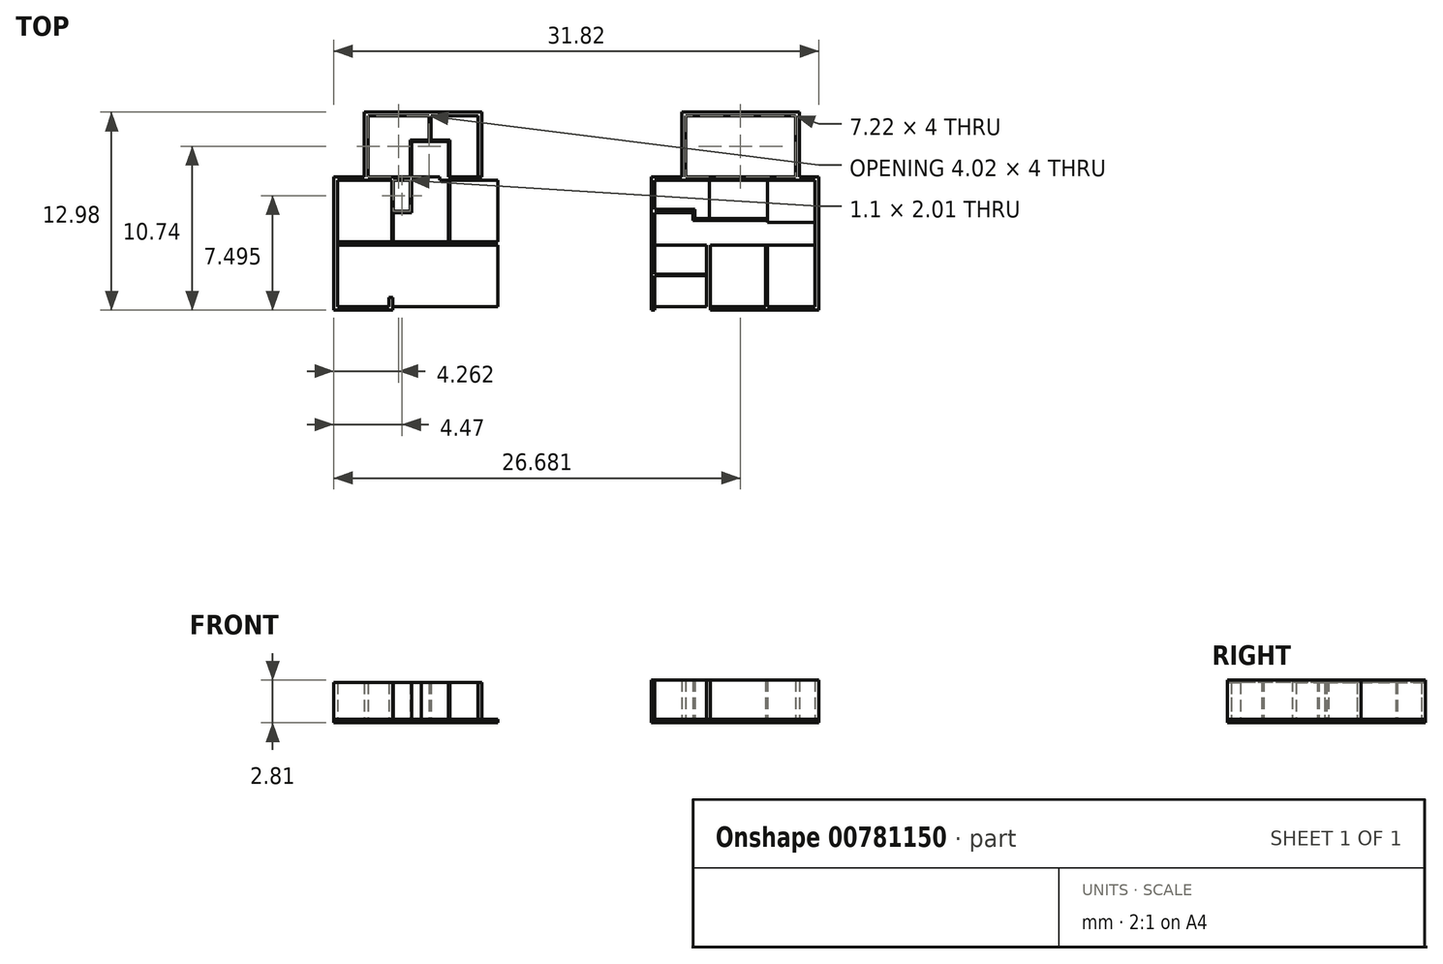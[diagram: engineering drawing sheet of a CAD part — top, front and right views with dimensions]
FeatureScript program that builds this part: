
annotation { "Feature Type Name" : "Feature", "Feature Type Description" : "" }
export const myFeature = defineFeature(function(context is Context, id is Id, definition is map)
    precondition{}
    {
        {
            var Q0;
            Q0=qCreatedBy(makeId("Top.planeOp"),FACE);
            var sketch = newSketch(context, id + "F0", { "sketchPlane" : qUnion([Q0])});
            skLineSegment(sketch, "E0.bottom", {"start": v(-5.5, 4.37) * mm, "end": v(5.5, 4.37) * mm});
            skLineSegment(sketch, "E0.top", {"start": v(-5.5, -4.37) * mm, "end": v(5.5, -4.37) * mm});
            skLineSegment(sketch, "E0.left", {"start": v(-5.5, 4.37) * mm, "end": v(-5.5, -4.37) * mm});
            skLineSegment(sketch, "E0.right", {"start": v(5.5, 4.37) * mm, "end": v(5.5, -4.37) * mm});
            skPoint(sketch, "E0.middle", {"position": v(0, 0) * mm});
            skLineSegment(sketch, "E1.bottom", {"start": v(-5.25, 4.13) * mm, "end": v(5.25, 4.13) * mm});
            skLineSegment(sketch, "E1.top", {"start": v(-5.25, -4.13) * mm, "end": v(5.25, -4.13) * mm});
            skLineSegment(sketch, "E1.left", {"start": v(-5.25, 4.13) * mm, "end": v(-5.25, -4.13) * mm});
            skLineSegment(sketch, "E1.right", {"start": v(5.25, 4.13) * mm, "end": v(5.25, -4.13) * mm});
            skLineSegment(sketch, "E2.bottom", {"start": v(-5.5, -4.37) * mm, "end": v(-1.63, -4.37) * mm});
            skLineSegment(sketch, "E2.top", {"start": v(-5.5, -7.87) * mm, "end": v(-1.63, -7.87) * mm});
            skLineSegment(sketch, "E2.left", {"start": v(-5.5, -4.37) * mm, "end": v(-5.5, -7.87) * mm});
            skLineSegment(sketch, "E2.right", {"start": v(-1.63, -4.37) * mm, "end": v(-1.63, -7.87) * mm});
            skLineSegment(sketch, "E3.bottom", {"start": v(-5.25, -4.37) * mm, "end": v(-1.87, -4.37) * mm});
            skLineSegment(sketch, "E3.top", {"start": v(-5.25, -7.63) * mm, "end": v(-1.87, -7.63) * mm});
            skLineSegment(sketch, "E3.left", {"start": v(-5.25, -4.37) * mm, "end": v(-5.25, -7.63) * mm});
            skLineSegment(sketch, "E3.right", {"start": v(-1.87, -4.37) * mm, "end": v(-1.87, -7.63) * mm});
            skLineSegment(sketch, "E4", {"start": v(-5.25, 0.12) * mm, "end": v(5.25, 0.12) * mm});
            skLineSegment(sketch, "E5", {"start": v(5.25, 0.12) * mm, "end": v(5.25, -0.12) * mm});
            skLineSegment(sketch, "E6", {"start": v(5.25, -0.12) * mm, "end": v(-5.25, -0.12) * mm});
            skLineSegment(sketch, "E7", {"start": v(-5.25, -0.12) * mm, "end": v(-5.25, 0.12) * mm});
            skLineSegment(sketch, "E8.bottom", {"start": v(-1.63, -4.37) * mm, "end": v(-1.87, -4.37) * mm});
            skLineSegment(sketch, "E8.top", {"start": v(-1.63, -3.53) * mm, "end": v(-1.87, -3.53) * mm});
            skLineSegment(sketch, "E8.left", {"start": v(-1.63, -4.37) * mm, "end": v(-1.63, -3.53) * mm});
            skLineSegment(sketch, "E8.right", {"start": v(-1.87, -4.37) * mm, "end": v(-1.87, -3.53) * mm});
            skLineSegment(sketch, "E9", {"start": v(-5.25, -4.13) * mm, "end": v(-5.25, -4.37) * mm});
            skLineSegment(sketch, "E10", {"start": v(-1.87, -4.13) * mm, "end": v(-1.87, -4.37) * mm});
            skLineSegment(sketch, "E11.bottom", {"start": v(4.2, 4.37) * mm, "end": v(-3.49, 4.37) * mm});
            skLineSegment(sketch, "E11.top", {"start": v(4.2, 8.61) * mm, "end": v(-3.49, 8.61) * mm});
            skLineSegment(sketch, "E11.left", {"start": v(4.2, 4.37) * mm, "end": v(4.2, 8.61) * mm});
            skLineSegment(sketch, "E11.right", {"start": v(-3.49, 4.37) * mm, "end": v(-3.49, 8.61) * mm});
            skLineSegment(sketch, "E12.bottom", {"start": v(-3.25, 4.37) * mm, "end": v(3.97, 4.37) * mm});
            skLineSegment(sketch, "E12.top", {"start": v(-3.25, 8.37) * mm, "end": v(3.97, 8.37) * mm});
            skLineSegment(sketch, "E12.left", {"start": v(-3.25, 4.37) * mm, "end": v(-3.25, 8.37) * mm});
            skLineSegment(sketch, "E12.right", {"start": v(3.97, 4.37) * mm, "end": v(3.97, 8.37) * mm});
            skLineSegment(sketch, "E13", {"start": v(-1.68, 4.13) * mm, "end": v(-1.68, 0.12) * mm});
            skLineSegment(sketch, "E14", {"start": v(-1.68, 0.12) * mm, "end": v(-1.58, 0.12) * mm});
            skLineSegment(sketch, "E15", {"start": v(-1.58, 0.12) * mm, "end": v(-1.58, 4.13) * mm});
            skLineSegment(sketch, "E16", {"start": v(-1.58, 4.13) * mm, "end": v(2.02, 4.13) * mm});
            skLineSegment(sketch, "E17", {"start": v(2.02, 4.13) * mm, "end": v(2.02, 0.12) * mm});
            skLineSegment(sketch, "E18", {"start": v(2.02, 0.12) * mm, "end": v(2.12, 0.12) * mm});
            skLineSegment(sketch, "E19", {"start": v(2.12, 0.12) * mm, "end": v(2.12, 4.13) * mm});
            skLineSegment(sketch, "E20", {"start": v(2.12, 4.13) * mm, "end": v(2.02, 4.13) * mm});
            skLineSegment(sketch, "E21", {"start": v(-1.58, 4.13) * mm, "end": v(-1.68, 4.13) * mm});
            skLineSegment(sketch, "E22", {"start": v(-0.48, 4.13) * mm, "end": v(-0.48, 2.12) * mm});
            skLineSegment(sketch, "E23", {"start": v(-0.48, 2.12) * mm, "end": v(-1.58, 2.12) * mm});
            skLineSegment(sketch, "E24", {"start": v(-1.58, 2.12) * mm, "end": v(-1.58, 2.02) * mm});
            skLineSegment(sketch, "E25", {"start": v(-1.58, 2.02) * mm, "end": v(-0.38, 2.02) * mm});
            skLineSegment(sketch, "E26", {"start": v(-0.38, 2.02) * mm, "end": v(-0.38, 4.13) * mm});
            skLineSegment(sketch, "E27", {"start": v(-0.38, 4.13) * mm, "end": v(-0.48, 4.13) * mm});
            skLineSegment(sketch, "E28", {"start": v(1.45, 4.37) * mm, "end": v(1.45, 4.13) * mm});
            skLineSegment(sketch, "E29", {"start": v(0.25, 4.37) * mm, "end": v(0.25, 4.13) * mm});
            skLineSegment(sketch, "E30", {"start": v(2.12, 4.37) * mm, "end": v(2.12, 6.54) * mm});
            skLineSegment(sketch, "E31", {"start": v(-0.38, 4.37) * mm, "end": v(-0.48, 4.37) * mm});
            skLineSegment(sketch, "E32", {"start": v(-0.38, 6.67) * mm, "end": v(2.02, 6.67) * mm});
            skLineSegment(sketch, "E33", {"start": v(2.02, 6.67) * mm, "end": v(2.02, 4.37) * mm});
            skLineSegment(sketch, "E34", {"start": v(-0.48, 6.77) * mm, "end": v(2.12, 6.77) * mm});
            skLineSegment(sketch, "E35", {"start": v(2.12, 6.77) * mm, "end": v(2.12, 6.54) * mm});
            skLineSegment(sketch, "E36", {"start": v(0.87, 6.77) * mm, "end": v(0.87, 8.37) * mm});
            skLineSegment(sketch, "E37", {"start": v(0.87, 8.37) * mm, "end": v(0.77, 8.37) * mm});
            skLineSegment(sketch, "E38", {"start": v(0.77, 8.37) * mm, "end": v(0.77, 6.77) * mm});
            skLineSegment(sketch, "E39", {"start": v(-0.48, 6.77) * mm, "end": v(-0.49, 6.77) * mm});
            skLineSegment(sketch, "E40", {"start": v(-0.49, 6.77) * mm, "end": v(-0.49, 4.37) * mm});
            skLineSegment(sketch, "E41", {"start": v(-0.49, 4.37) * mm, "end": v(-0.39, 4.37) * mm});
            skLineSegment(sketch, "E42", {"start": v(-0.39, 4.37) * mm, "end": v(-0.39, 6.67) * mm});
            skLineSegment(sketch, "E43", {"start": v(-0.39, 6.67) * mm, "end": v(-0.38, 6.67) * mm});
            skLineSegment(sketch, "E44.bottom", {"start": v(15.33, 4.37) * mm, "end": v(26.32, 4.37) * mm});
            skLineSegment(sketch, "E44.top", {"start": v(15.33, -4.37) * mm, "end": v(26.32, -4.37) * mm});
            skLineSegment(sketch, "E44.left", {"start": v(15.33, 4.37) * mm, "end": v(15.33, -4.37) * mm});
            skLineSegment(sketch, "E44.right", {"start": v(26.32, 4.37) * mm, "end": v(26.32, -4.37) * mm});
            skPoint(sketch, "E44.middle", {"position": v(20.82, 0) * mm});
            skLineSegment(sketch, "E45.bottom", {"start": v(15.57, 4.13) * mm, "end": v(26.08, 4.13) * mm});
            skLineSegment(sketch, "E45.top", {"start": v(15.57, -4.13) * mm, "end": v(26.08, -4.13) * mm});
            skLineSegment(sketch, "E45.left", {"start": v(15.57, 4.13) * mm, "end": v(15.57, -4.13) * mm});
            skLineSegment(sketch, "E45.right", {"start": v(26.08, 4.13) * mm, "end": v(26.08, -4.13) * mm});
            skLineSegment(sketch, "E46.bottom", {"start": v(15.33, -4.37) * mm, "end": v(19.2, -4.37) * mm});
            skLineSegment(sketch, "E46.top", {"start": v(15.33, -7.87) * mm, "end": v(19.2, -7.87) * mm});
            skLineSegment(sketch, "E46.left", {"start": v(15.33, -4.37) * mm, "end": v(15.33, -7.87) * mm});
            skLineSegment(sketch, "E46.right", {"start": v(19.2, -4.37) * mm, "end": v(19.2, -7.87) * mm});
            skLineSegment(sketch, "E47.bottom", {"start": v(15.57, -4.37) * mm, "end": v(18.95, -4.37) * mm});
            skLineSegment(sketch, "E47.top", {"start": v(15.57, -7.63) * mm, "end": v(18.95, -7.63) * mm});
            skLineSegment(sketch, "E47.left", {"start": v(15.57, -4.37) * mm, "end": v(15.57, -7.63) * mm});
            skLineSegment(sketch, "E47.right", {"start": v(18.95, -4.37) * mm, "end": v(18.95, -7.63) * mm});
            skLineSegment(sketch, "E48", {"start": v(15.57, 0.12) * mm, "end": v(26.08, 0.12) * mm});
            skLineSegment(sketch, "E49", {"start": v(26.08, 0.12) * mm, "end": v(26.08, -0.12) * mm});
            skLineSegment(sketch, "E50", {"start": v(26.08, -0.12) * mm, "end": v(15.57, -0.12) * mm});
            skLineSegment(sketch, "E51", {"start": v(15.57, -0.12) * mm, "end": v(15.57, 0.12) * mm});
            skLineSegment(sketch, "E52.bottom", {"start": v(19.2, -4.37) * mm, "end": v(18.95, -4.37) * mm});
            skLineSegment(sketch, "E52.top", {"start": v(19.2, -0.12) * mm, "end": v(18.95, -0.12) * mm});
            skLineSegment(sketch, "E52.left", {"start": v(19.2, -4.37) * mm, "end": v(19.2, -0.12) * mm});
            skLineSegment(sketch, "E52.right", {"start": v(18.95, -4.37) * mm, "end": v(18.95, -0.12) * mm});
            skLineSegment(sketch, "E53", {"start": v(15.57, -4.13) * mm, "end": v(15.57, -4.37) * mm});
            skLineSegment(sketch, "E54", {"start": v(18.95, -4.13) * mm, "end": v(18.95, -4.37) * mm});
            skLineSegment(sketch, "E55.bottom", {"start": v(25.03, 4.37) * mm, "end": v(17.33, 4.37) * mm});
            skLineSegment(sketch, "E55.top", {"start": v(25.03, 8.61) * mm, "end": v(17.33, 8.61) * mm});
            skLineSegment(sketch, "E55.left", {"start": v(25.03, 4.37) * mm, "end": v(25.03, 8.61) * mm});
            skLineSegment(sketch, "E55.right", {"start": v(17.33, 4.37) * mm, "end": v(17.33, 8.61) * mm});
            skLineSegment(sketch, "E56.bottom", {"start": v(17.57, 4.37) * mm, "end": v(24.8, 4.37) * mm});
            skLineSegment(sketch, "E56.top", {"start": v(17.57, 8.37) * mm, "end": v(24.8, 8.37) * mm});
            skLineSegment(sketch, "E56.left", {"start": v(17.57, 4.37) * mm, "end": v(17.57, 8.37) * mm});
            skLineSegment(sketch, "E56.right", {"start": v(24.8, 4.37) * mm, "end": v(24.8, 8.37) * mm});
            skLineSegment(sketch, "E57", {"start": v(19.14, 0.12) * mm, "end": v(19.24, 0.12) * mm});
            skLineSegment(sketch, "E58", {"start": v(19.24, 4.13) * mm, "end": v(22.84, 4.13) * mm});
            skLineSegment(sketch, "E59", {"start": v(22.84, 0.12) * mm, "end": v(22.94, 0.12) * mm});
            skLineSegment(sketch, "E60", {"start": v(22.94, 4.13) * mm, "end": v(22.84, 4.13) * mm});
            skLineSegment(sketch, "E61", {"start": v(19.24, 4.13) * mm, "end": v(19.14, 4.13) * mm});
            skLineSegment(sketch, "E62", {"start": v(20.44, 4.13) * mm, "end": v(20.34, 4.13) * mm});
            skLineSegment(sketch, "E63", {"start": v(20.44, 4.37) * mm, "end": v(20.34, 4.37) * mm});
            skLineSegment(sketch, "E64", {"start": v(21.7, 6.77) * mm, "end": v(21.7, 8.37) * mm});
            skLineSegment(sketch, "E65", {"start": v(21.7, 8.37) * mm, "end": v(21.59, 8.37) * mm});
            skLineSegment(sketch, "E66", {"start": v(21.59, 8.37) * mm, "end": v(21.59, 6.77) * mm});
            skLineSegment(sketch, "E67", {"start": v(20.33, 4.37) * mm, "end": v(20.43, 4.37) * mm});
            skLineSegment(sketch, "E68", {"start": v(22.94, -4.13) * mm, "end": v(22.94, -0.12) * mm});
            skLineSegment(sketch, "E69", {"start": v(22.94, -0.12) * mm, "end": v(22.83, -0.12) * mm});
            skLineSegment(sketch, "E70", {"start": v(22.83, -0.12) * mm, "end": v(22.83, -4.13) * mm});
            skLineSegment(sketch, "E71", {"start": v(22.94, 4.13) * mm, "end": v(22.94, 1.37) * mm});
            skLineSegment(sketch, "E72", {"start": v(22.94, 1.37) * mm, "end": v(26.08, 1.37) * mm});
            skLineSegment(sketch, "E73", {"start": v(26.08, 1.37) * mm, "end": v(26.08, 1.25) * mm});
            skLineSegment(sketch, "E74", {"start": v(26.08, 1.25) * mm, "end": v(22.83, 1.25) * mm});
            skLineSegment(sketch, "E75", {"start": v(22.83, 1.25) * mm, "end": v(22.83, 4.13) * mm});
            skLineSegment(sketch, "E76", {"start": v(15.57, 2.01) * mm, "end": v(18.06, 2.01) * mm});
            skLineSegment(sketch, "E77", {"start": v(18.06, 2.01) * mm, "end": v(18.06, 1.52) * mm});
            skLineSegment(sketch, "E78", {"start": v(18.06, 1.52) * mm, "end": v(22.83, 1.52) * mm});
            skLineSegment(sketch, "E79", {"start": v(22.83, 1.52) * mm, "end": v(22.83, 1.63) * mm});
            skLineSegment(sketch, "E80", {"start": v(22.83, 1.63) * mm, "end": v(18.18, 1.63) * mm});
            skLineSegment(sketch, "E81", {"start": v(18.18, 1.63) * mm, "end": v(18.18, 2.25) * mm});
            skLineSegment(sketch, "E82", {"start": v(18.18, 2.25) * mm, "end": v(15.57, 2.25) * mm});
            skLineSegment(sketch, "E83", {"start": v(19.13, 4.13) * mm, "end": v(19.13, 1.63) * mm});
            skLineSegment(sketch, "E84", {"start": v(19.13, 1.63) * mm, "end": v(19.24, 1.63) * mm});
            skLineSegment(sketch, "E85", {"start": v(19.24, 1.63) * mm, "end": v(19.24, 4.13) * mm});
            skLineSegment(sketch, "E86", {"start": v(15.57, -2) * mm, "end": v(18.95, -2) * mm});
            skLineSegment(sketch, "E87", {"start": v(18.95, -2) * mm, "end": v(18.95, -2.12) * mm});
            skLineSegment(sketch, "E88", {"start": v(18.95, -2.12) * mm, "end": v(15.57, -2.12) * mm});
            skSolve(sketch);
        }
        {
            var Q0;
            {var subQ0=sQuery(id+"F0.wireOp",EDGE,"E12.left");Q0=makeQuery(id+"F0.imprint","IMPRINT",FACE,{"disambiguationData":[TD([[makeQuery(id+"F0.imprint","IMPRINT",EDGE,{"derivedFrom":subQ0}),-1.0]])]});}
            var Q1;
            {var subQ3=sQuery(id+"F0.wireOp",EDGE,"E13");Q1=makeQuery(id+"F0.imprint","IMPRINT",FACE,{"disambiguationData":[TD([[makeQuery(id+"F0.imprint","IMPRINT",EDGE,{"derivedFrom":subQ3}),-1.0]])]});}
            var Q2;
            {var subQ3=sQuery(id+"F0.wireOp",EDGE,"E31");Q2=makeQuery(id+"F0.imprint","IMPRINT",FACE,{"disambiguationData":[TD([[makeQuery(id+"F0.imprint","IMPRINT",EDGE,{"derivedFrom":subQ3}),-1.0]])]});}
            var Q3;
            {var subQ1=sQuery(id+"F0.wireOp",EDGE,"E12.right");Q3=makeQuery(id+"F0.imprint","IMPRINT",FACE,{"disambiguationData":[TD([[makeQuery(id+"F0.imprint","IMPRINT",EDGE,{"derivedFrom":subQ1}),1.0]])]});}
            var Q4;
            {var subQ3=sQuery(id+"F0.wireOp",EDGE,"E19");Q4=makeQuery(id+"F0.imprint","IMPRINT",FACE,{"disambiguationData":[TD([[makeQuery(id+"F0.imprint","IMPRINT",EDGE,{"derivedFrom":subQ3}),-1.0]])]});}
            var Q5;
            {var subQ3=sQuery(id+"F0.wireOp",EDGE,"E6");Q5=makeQuery(id+"F0.imprint","IMPRINT",FACE,{"disambiguationData":[TD([[makeQuery(id+"F0.imprint","IMPRINT",EDGE,{"derivedFrom":subQ3}),1.0]])]});}
            var Q6;
            Q6=makeQuery(id+"F0.imprint","IMPRINT",FACE,{"disambiguationData":[TD([[makeQuery(id+"F0.imprint","IMPRINT",EDGE,{"derivedFrom":sQuery(id+"F0.wireOp",EDGE,"E3.bottom")}),-1.0]])]});
            var Q7;
            Q7=makeQuery(id+"F0.imprint","IMPRINT",FACE,{"disambiguationData":[TD([[makeQuery(id+"F0.imprint","IMPRINT",EDGE,{"derivedFrom":sQuery(id+"F0.wireOp",EDGE,"E2.bottom")}),-1.0]])]});
            var Q8;
            {var subQ1=sQuery(id+"F0.wireOp",EDGE,"E0.top");Q8=makeQuery(id+"F0.imprint","IMPRINT",FACE,{"disambiguationData":[TD([[makeQuery(id+"F0.imprint","IMPRINT",EDGE,{"derivedFrom":subQ1}),1.0]])]});}
            var Q9;
            {var subQ10=sQuery(id+"F0.wireOp",EDGE,"E0.left");Q9=makeQuery(id+"F0.imprint","IMPRINT",FACE,{"disambiguationData":[TD([[makeQuery(id+"F0.imprint","IMPRINT",EDGE,{"derivedFrom":subQ10}),1.0]])]});}
            var Q10;
            Q10=makeQuery(id+"F0.imprint","IMPRINT",FACE,{"disambiguationData":[TD([[makeQuery(id+"F0.imprint","IMPRINT",EDGE,{"derivedFrom":sQuery(id+"F0.wireOp",EDGE,"E3.bottom")}),1.0]])]});
            var Q11;
            {var subQ4=sQuery(id+"F0.wireOp",EDGE,"E8.top");Q11=makeQuery(id+"F0.imprint","IMPRINT",FACE,{"disambiguationData":[TD([[makeQuery(id+"F0.imprint","IMPRINT",EDGE,{"derivedFrom":subQ4}),1.0]])]});}
            var Q12;
            {var subQ4=sQuery(id+"F0.wireOp",EDGE,"E22");Q12=makeQuery(id+"F0.imprint","IMPRINT",FACE,{"disambiguationData":[TD([[makeQuery(id+"F0.imprint","IMPRINT",EDGE,{"derivedFrom":subQ4}),-1.0]])]});}
            var Q13;
            {var subQ0=sQuery(id+"F0.wireOp",EDGE,"E28");Q13=makeQuery(id+"F0.imprint","IMPRINT",FACE,{"disambiguationData":[TD([[makeQuery(id+"F0.imprint","IMPRINT",EDGE,{"derivedFrom":subQ0}),-1.0]])]});}
            var Q14;
            Q14=makeQuery(id+"F0.imprint","IMPRINT",FACE,{"disambiguationData":[TD([[makeQuery(id+"F0.imprint","IMPRINT",EDGE,{"derivedFrom":sQuery(id+"F0.wireOp",EDGE,"E11.top")}),1.0]])]});
            var Q15;
            {var subQ4=sQuery(id+"F0.wireOp",EDGE,"E8.bottom");Q15=makeQuery(id+"F0.imprint","IMPRINT",FACE,{"disambiguationData":[TD([[makeQuery(id+"F0.imprint","IMPRINT",EDGE,{"derivedFrom":subQ4}),-1.0]])]});}
            var Q16;
            {var subQ0=sQuery(id+"F0.wireOp",EDGE,"E5");Q16=makeQuery(id+"F0.imprint","IMPRINT",FACE,{"disambiguationData":[TD([[makeQuery(id+"F0.imprint","IMPRINT",EDGE,{"derivedFrom":subQ0}),-1.0]])]});}
            var Q17;
            {var subQ6=sQuery(id+"F0.wireOp",EDGE,"E17");Q17=makeQuery(id+"F0.imprint","IMPRINT",FACE,{"disambiguationData":[TD([[makeQuery(id+"F0.imprint","IMPRINT",EDGE,{"derivedFrom":subQ6}),-1.0]])]});}
            var Q18;
            Q18=makeQuery(id+"F0.imprint","IMPRINT",FACE,{"disambiguationData":[TD([[makeQuery(id+"F0.imprint","IMPRINT",EDGE,{"derivedFrom":sQuery(id+"F0.wireOp",EDGE,"E22")}),1.0]])]});
            var Q19;
            Q19=makeQuery(id+"F0.imprint","IMPRINT",FACE,{"disambiguationData":[TD([[makeQuery(id+"F0.imprint","IMPRINT",EDGE,{"derivedFrom":sQuery(id+"F0.wireOp",EDGE,"E13")}),1.0]])]});
            var Q20;
            {var subQ6=sQuery(id+"F0.wireOp",EDGE,"E30");Q20=makeQuery(id+"F0.imprint","IMPRINT",FACE,{"disambiguationData":[TD([[makeQuery(id+"F0.imprint","IMPRINT",EDGE,{"derivedFrom":subQ6}),1.0]])]});}
            var Q21;
            Q21=makeQuery(id+"F0.imprint","IMPRINT",FACE,{"disambiguationData":[TD([[makeQuery(id+"F0.imprint","IMPRINT",EDGE,{"derivedFrom":sQuery(id+"F0.wireOp",EDGE,"E17")}),1.0]])]});
            var Q22;
            {var subQ0=sQuery(id+"F0.wireOp",EDGE,"E36");Q22=makeQuery(id+"F0.imprint","IMPRINT",FACE,{"disambiguationData":[TD([[makeQuery(id+"F0.imprint","IMPRINT",EDGE,{"derivedFrom":subQ0}),1.0]])]});}
            var Q23;
            {var subQ4=sQuery(id+"F0.wireOp",EDGE,"E56.left");Q23=makeQuery(id+"F0.imprint","IMPRINT",FACE,{"disambiguationData":[TD([[makeQuery(id+"F0.imprint","IMPRINT",EDGE,{"derivedFrom":subQ4}),-1.0]])]});}
            var Q24;
            {var subQ0=sQuery(id+"F0.wireOp",EDGE,"E81");Q24=makeQuery(id+"F0.imprint","IMPRINT",FACE,{"disambiguationData":[TD([[makeQuery(id+"F0.imprint","IMPRINT",EDGE,{"derivedFrom":subQ0}),-1.0]])]});}
            var Q25;
            {var subQ6=sQuery(id+"F0.wireOp",EDGE,"E62");Q25=makeQuery(id+"F0.imprint","IMPRINT",FACE,{"disambiguationData":[TD([[makeQuery(id+"F0.imprint","IMPRINT",EDGE,{"derivedFrom":subQ6}),1.0]])]});}
            var Q26;
            {var subQ7=sQuery(id+"F0.wireOp",EDGE,"E57");Q26=makeQuery(id+"F0.imprint","IMPRINT",FACE,{"disambiguationData":[TD([[makeQuery(id+"F0.imprint","IMPRINT",EDGE,{"derivedFrom":subQ7}),1.0]])]});}
            var Q27;
            {var subQ0=sQuery(id+"F0.wireOp",EDGE,"E70");Q27=makeQuery(id+"F0.imprint","IMPRINT",FACE,{"disambiguationData":[TD([[makeQuery(id+"F0.imprint","IMPRINT",EDGE,{"derivedFrom":subQ0}),-1.0]])]});}
            var Q28;
            {var subQ3=sQuery(id+"F0.wireOp",EDGE,"E86");Q28=makeQuery(id+"F0.imprint","IMPRINT",FACE,{"disambiguationData":[TD([[makeQuery(id+"F0.imprint","IMPRINT",EDGE,{"derivedFrom":subQ3}),1.0]])]});}
            var Q29;
            {var subQ8=sQuery(id+"F0.wireOp",EDGE,"E87");Q29=makeQuery(id+"F0.imprint","IMPRINT",FACE,{"disambiguationData":[TD([[makeQuery(id+"F0.imprint","IMPRINT",EDGE,{"derivedFrom":subQ8}),1.0]])]});}
            var Q30;
            {var subQ10=sQuery(id+"F0.wireOp",EDGE,"E49");Q30=makeQuery(id+"F0.imprint","IMPRINT",FACE,{"disambiguationData":[TD([[makeQuery(id+"F0.imprint","IMPRINT",EDGE,{"derivedFrom":subQ10}),-1.0]])]});}
            var Q31;
            {var subQ0=sQuery(id+"F0.wireOp",EDGE,"E76");Q31=makeQuery(id+"F0.imprint","IMPRINT",FACE,{"disambiguationData":[TD([[makeQuery(id+"F0.imprint","IMPRINT",EDGE,{"derivedFrom":subQ0}),1.0]])]});}
            var Q32;
            {var subQ30=sQuery(id+"F0.wireOp",EDGE,"E44.top");Q32=makeQuery(id+"F0.imprint","IMPRINT",FACE,{"disambiguationData":[TD([[makeQuery(id+"F0.imprint","IMPRINT",EDGE,{"derivedFrom":subQ30}),1.0]])]});}
            var Q33;
            Q33=makeQuery(id+"F0.imprint","IMPRINT",FACE,{"disambiguationData":[TD([[makeQuery(id+"F0.imprint","IMPRINT",EDGE,{"derivedFrom":sQuery(id+"F0.wireOp",EDGE,"E55.top")}),1.0]])]});
            var Q34;
            Q34=makeQuery(id+"F0.imprint","IMPRINT",FACE,{"disambiguationData":[TD([[makeQuery(id+"F0.imprint","IMPRINT",EDGE,{"derivedFrom":sQuery(id+"F0.wireOp",EDGE,"E47.bottom")}),1.0]])]});
            var Q35;
            {var subQ5=sQuery(id+"F0.wireOp",EDGE,"E88");Q35=makeQuery(id+"F0.imprint","IMPRINT",FACE,{"disambiguationData":[TD([[makeQuery(id+"F0.imprint","IMPRINT",EDGE,{"derivedFrom":subQ5}),1.0]])]});}
            var Q36;
            Q36=makeQuery(id+"F0.imprint","IMPRINT",FACE,{"disambiguationData":[TD([[makeQuery(id+"F0.imprint","IMPRINT",EDGE,{"derivedFrom":sQuery(id+"F0.wireOp",EDGE,"E47.bottom")}),-1.0]])]});
            var Q37;
            Q37=makeQuery(id+"F0.imprint","IMPRINT",FACE,{"disambiguationData":[TD([[makeQuery(id+"F0.imprint","IMPRINT",EDGE,{"derivedFrom":sQuery(id+"F0.wireOp",EDGE,"E46.bottom")}),-1.0]])]});
            var Q38;
            {var subQ0=sQuery(id+"F0.wireOp",EDGE,"E86");Q38=makeQuery(id+"F0.imprint","IMPRINT",FACE,{"disambiguationData":[TD([[makeQuery(id+"F0.imprint","IMPRINT",EDGE,{"derivedFrom":subQ0}),-1.0]])]});}
            var Q39;
            {var subQ4=sQuery(id+"F0.wireOp",EDGE,"E52.bottom");Q39=makeQuery(id+"F0.imprint","IMPRINT",FACE,{"disambiguationData":[TD([[makeQuery(id+"F0.imprint","IMPRINT",EDGE,{"derivedFrom":subQ4}),-1.0]])]});}
            var Q40;
            {var subQ1=sQuery(id+"F0.wireOp",EDGE,"E61");Q40=makeQuery(id+"F0.imprint","IMPRINT",FACE,{"disambiguationData":[TD([[makeQuery(id+"F0.imprint","IMPRINT",EDGE,{"derivedFrom":subQ1}),1.0]])]});}
            var Q41;
            {var subQ3=sQuery(id+"F0.wireOp",EDGE,"E71");Q41=makeQuery(id+"F0.imprint","IMPRINT",FACE,{"disambiguationData":[TD([[makeQuery(id+"F0.imprint","IMPRINT",EDGE,{"derivedFrom":subQ3}),1.0]])]});}
            var Q42;
            {var subQ3=sQuery(id+"F0.wireOp",EDGE,"E68");Q42=makeQuery(id+"F0.imprint","IMPRINT",FACE,{"disambiguationData":[TD([[makeQuery(id+"F0.imprint","IMPRINT",EDGE,{"derivedFrom":subQ3}),-1.0]])]});}
            var Q43;
            {var subQ0=sQuery(id+"F0.wireOp",EDGE,"E68");Q43=makeQuery(id+"F0.imprint","IMPRINT",FACE,{"disambiguationData":[TD([[makeQuery(id+"F0.imprint","IMPRINT",EDGE,{"derivedFrom":subQ0}),1.0]])]});}
            var Q44;
            {var subQ0=sQuery(id+"F0.wireOp",EDGE,"E60");Q44=makeQuery(id+"F0.imprint","IMPRINT",FACE,{"disambiguationData":[TD([[makeQuery(id+"F0.imprint","IMPRINT",EDGE,{"derivedFrom":subQ0}),1.0]])]});}
            extrude(context, id + "F1", {"entities" : qUnion([Q0, Q1, Q2, Q3, Q4, Q5, Q6, Q7, Q8, Q9, Q10, Q11, Q12, Q13, Q14, Q15, Q16, Q17, Q18, Q19, Q20, Q21, Q22, Q23, Q24, Q25, Q26, Q27, Q28, Q29, Q30, Q31, Q32, Q33, Q34, Q35, Q36, Q37, Q38, Q39, Q40, Q41, Q42, Q43, Q44]), "oppositeDirection" : true, "depth" : 0.25 * mm, "offsetDistance" : 25 * mm});
        }
        {
            var Q0;
            {var subQ30=sQuery(id+"F0.wireOp",EDGE,"E44.top");Q0=makeQuery(id+"F0.imprint","IMPRINT",FACE,{"disambiguationData":[TD([[makeQuery(id+"F0.imprint","IMPRINT",EDGE,{"derivedFrom":subQ30}),1.0]])]});}
            var Q1;
            {var subQ0=sQuery(id+"F0.wireOp",EDGE,"E76");Q1=makeQuery(id+"F0.imprint","IMPRINT",FACE,{"disambiguationData":[TD([[makeQuery(id+"F0.imprint","IMPRINT",EDGE,{"derivedFrom":subQ0}),1.0]])]});}
            var Q2;
            {var subQ4=sQuery(id+"F0.wireOp",EDGE,"E52.bottom");Q2=makeQuery(id+"F0.imprint","IMPRINT",FACE,{"disambiguationData":[TD([[makeQuery(id+"F0.imprint","IMPRINT",EDGE,{"derivedFrom":subQ4}),-1.0]])]});}
            var Q3;
            {var subQ1=sQuery(id+"F0.wireOp",EDGE,"E61");Q3=makeQuery(id+"F0.imprint","IMPRINT",FACE,{"disambiguationData":[TD([[makeQuery(id+"F0.imprint","IMPRINT",EDGE,{"derivedFrom":subQ1}),1.0]])]});}
            var Q4;
            {var subQ0=sQuery(id+"F0.wireOp",EDGE,"E60");Q4=makeQuery(id+"F0.imprint","IMPRINT",FACE,{"disambiguationData":[TD([[makeQuery(id+"F0.imprint","IMPRINT",EDGE,{"derivedFrom":subQ0}),1.0]])]});}
            var Q5;
            {var subQ0=sQuery(id+"F0.wireOp",EDGE,"E68");Q5=makeQuery(id+"F0.imprint","IMPRINT",FACE,{"disambiguationData":[TD([[makeQuery(id+"F0.imprint","IMPRINT",EDGE,{"derivedFrom":subQ0}),1.0]])]});}
            var Q6;
            {var subQ10=sQuery(id+"F0.wireOp",EDGE,"E49");Q6=makeQuery(id+"F0.imprint","IMPRINT",FACE,{"disambiguationData":[TD([[makeQuery(id+"F0.imprint","IMPRINT",EDGE,{"derivedFrom":subQ10}),-1.0]])]});}
            var Q7;
            {var subQ0=sQuery(id+"F0.wireOp",EDGE,"E86");Q7=makeQuery(id+"F0.imprint","IMPRINT",FACE,{"disambiguationData":[TD([[makeQuery(id+"F0.imprint","IMPRINT",EDGE,{"derivedFrom":subQ0}),-1.0]])]});}
            var Q8;
            Q8=makeQuery(id+"F0.imprint","IMPRINT",FACE,{"disambiguationData":[TD([[makeQuery(id+"F0.imprint","IMPRINT",EDGE,{"derivedFrom":sQuery(id+"F0.wireOp",EDGE,"E46.bottom")}),-1.0]])]});
            var Q9;
            Q9=makeQuery(id+"F0.imprint","IMPRINT",FACE,{"disambiguationData":[TD([[makeQuery(id+"F0.imprint","IMPRINT",EDGE,{"derivedFrom":sQuery(id+"F0.wireOp",EDGE,"E55.top")}),1.0]])]});
            extrude(context, id + "F2", {"entities" : qUnion([Q0, Q1, Q2, Q3, Q4, Q5, Q6, Q7, Q8, Q9]), "depth" : 2.56 * mm, "offsetDistance" : 25 * mm});
        }
        {
            var Q0;
            Q0=makeQuery(id+"F0.imprint","IMPRINT",FACE,{"disambiguationData":[TD([[makeQuery(id+"F0.imprint","IMPRINT",EDGE,{"derivedFrom":sQuery(id+"F0.wireOp",EDGE,"E11.top")}),1.0]])]});
            var Q1;
            {var subQ1=sQuery(id+"F0.wireOp",EDGE,"E0.top");Q1=makeQuery(id+"F0.imprint","IMPRINT",FACE,{"disambiguationData":[TD([[makeQuery(id+"F0.imprint","IMPRINT",EDGE,{"derivedFrom":subQ1}),1.0]])]});}
            var Q2;
            {var subQ10=sQuery(id+"F0.wireOp",EDGE,"E0.left");Q2=makeQuery(id+"F0.imprint","IMPRINT",FACE,{"disambiguationData":[TD([[makeQuery(id+"F0.imprint","IMPRINT",EDGE,{"derivedFrom":subQ10}),1.0]])]});}
            var Q3;
            Q3=makeQuery(id+"F0.imprint","IMPRINT",FACE,{"disambiguationData":[TD([[makeQuery(id+"F0.imprint","IMPRINT",EDGE,{"derivedFrom":sQuery(id+"F0.wireOp",EDGE,"E2.bottom")}),-1.0]])]});
            var Q4;
            {var subQ4=sQuery(id+"F0.wireOp",EDGE,"E8.bottom");Q4=makeQuery(id+"F0.imprint","IMPRINT",FACE,{"disambiguationData":[TD([[makeQuery(id+"F0.imprint","IMPRINT",EDGE,{"derivedFrom":subQ4}),-1.0]])]});}
            var Q5;
            {var subQ4=sQuery(id+"F0.wireOp",EDGE,"E8.top");Q5=makeQuery(id+"F0.imprint","IMPRINT",FACE,{"disambiguationData":[TD([[makeQuery(id+"F0.imprint","IMPRINT",EDGE,{"derivedFrom":subQ4}),1.0]])]});}
            var Q6;
            {var subQ0=sQuery(id+"F0.wireOp",EDGE,"E5");Q6=makeQuery(id+"F0.imprint","IMPRINT",FACE,{"disambiguationData":[TD([[makeQuery(id+"F0.imprint","IMPRINT",EDGE,{"derivedFrom":subQ0}),-1.0]])]});}
            var Q7;
            Q7=makeQuery(id+"F0.imprint","IMPRINT",FACE,{"disambiguationData":[TD([[makeQuery(id+"F0.imprint","IMPRINT",EDGE,{"derivedFrom":sQuery(id+"F0.wireOp",EDGE,"E13")}),1.0]])]});
            var Q8;
            Q8=makeQuery(id+"F0.imprint","IMPRINT",FACE,{"disambiguationData":[TD([[makeQuery(id+"F0.imprint","IMPRINT",EDGE,{"derivedFrom":sQuery(id+"F0.wireOp",EDGE,"E17")}),1.0]])]});
            var Q9;
            Q9=makeQuery(id+"F0.imprint","IMPRINT",FACE,{"disambiguationData":[TD([[makeQuery(id+"F0.imprint","IMPRINT",EDGE,{"derivedFrom":sQuery(id+"F0.wireOp",EDGE,"E22")}),1.0]])]});
            var Q10;
            {var subQ6=sQuery(id+"F0.wireOp",EDGE,"E30");Q10=makeQuery(id+"F0.imprint","IMPRINT",FACE,{"disambiguationData":[TD([[makeQuery(id+"F0.imprint","IMPRINT",EDGE,{"derivedFrom":subQ6}),1.0]])]});}
            var Q11;
            {var subQ0=sQuery(id+"F0.wireOp",EDGE,"E36");Q11=makeQuery(id+"F0.imprint","IMPRINT",FACE,{"disambiguationData":[TD([[makeQuery(id+"F0.imprint","IMPRINT",EDGE,{"derivedFrom":subQ0}),1.0]])]});}
            extrude(context, id + "F3", {"entities" : qUnion([Q0, Q1, Q2, Q3, Q4, Q5, Q6, Q7, Q8, Q9, Q10, Q11]), "depth" : 2.4 * mm, "offsetDistance" : 25 * mm});
        }
    });
